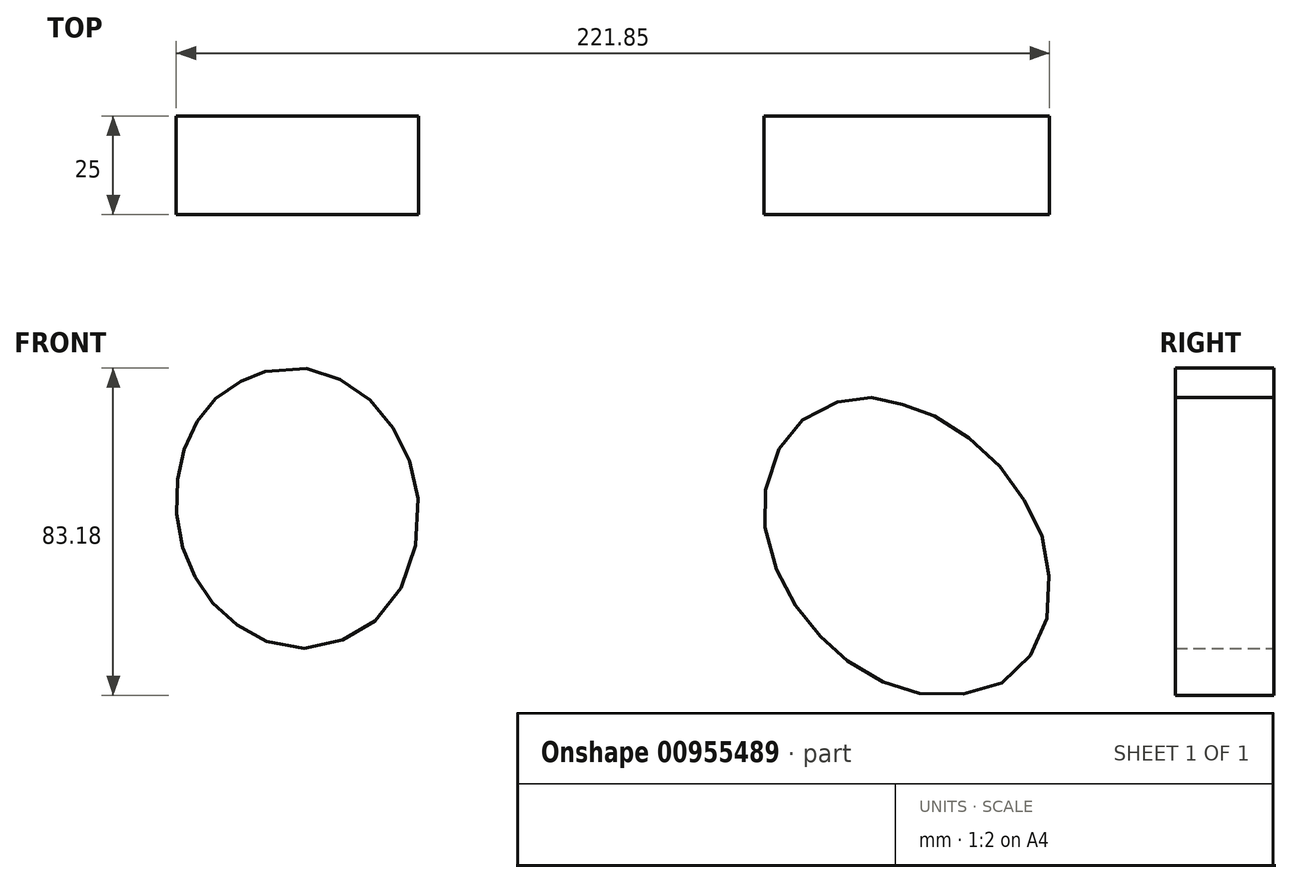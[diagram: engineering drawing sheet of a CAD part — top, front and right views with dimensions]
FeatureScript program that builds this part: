
annotation { "Feature Type Name" : "Feature", "Feature Type Description" : "" }
export const myFeature = defineFeature(function(context is Context, id is Id, definition is map)
    precondition{}
    {
        {
            var Q0;
            Q0=qCreatedBy(makeId("Front.planeOp"),FACE);
            var sketch = newSketch(context, id + "F0", { "sketchPlane" : qUnion([Q0])});
            skFitSpline(sketch, "E0", {"points": [v(238.48, -22.57) * mm, v(233.05, -23.03) * mm, v(227.5, -24.42) * mm, v(220.92, -28.35) * mm, v(216.76, -32.63) * mm, v(212.95, -40.48) * mm, v(211.33, -48) * mm, v(211.33, -54.46) * mm, v(213.18, -62.66) * mm, v(216.3, -70.52) * mm, v(220.23, -76.87) * mm, v(224.97, -82.53) * mm, v(229.47, -87.04) * mm, v(234.44, -90.85) * mm, v(241.72, -94.9) * mm, v(247.73, -97.2) * mm, v(256.04, -98.25) * mm, v(264.94, -97.44) * mm, v(271.64, -95.01) * mm, v(277.3, -90.16) * mm, v(281.11, -84.38) * mm, v(283.54, -76.3) * mm, v(283.54, -67.86) * mm, v(282.5, -60.12) * mm, v(279.84, -53.19) * mm, v(276.03, -46.72) * mm, v(271.3, -40.37) * mm, v(265.63, -34.82) * mm, v(258.47, -29.28) * mm, v(252.98, -26.66) * mm, v(247.84, -24.77) * mm, v(243.01, -23.3) * mm, v(238.48, -22.57) * mm]});
            skFitSpline(sketch, "E1", {"points": [v(84.5, -15.93) * mm, v(80.8, -17.29) * mm, v(74.78, -20.5) * mm, v(70.9, -23.8) * mm, v(67.1, -28.75) * mm, v(64.38, -34.58) * mm, v(62.73, -39.83) * mm, v(61.95, -47.99) * mm, v(62.25, -55.37) * mm, v(64.29, -62.95) * mm, v(67, -68.78) * mm, v(70.7, -74.22) * mm, v(75.94, -79.27) * mm, v(81.97, -83.15) * mm, v(90.61, -86.17) * mm, v(101.2, -85.1) * mm, v(109.65, -81.4) * mm, v(117.43, -73.44) * mm, v(122.48, -61.49) * mm, v(123.16, -47.01) * mm, v(120.73, -37.69) * mm, v(116.45, -29.53) * mm, v(110.92, -23.02) * mm, v(103.53, -18.06) * mm, v(95.96, -15.25) * mm, v(84.5, -15.93) * mm]});
            skSolve(sketch);
        }
        {
            var Q0;
            Q0 = qSketchRegion(id + "F0", true);
            extrude(context, id + "F1", {"entities" : qUnion([Q0]), "depth" : 25 * mm, "offsetDistance" : 25 * mm});
        }
    });
